# Revit family: Hager-GOLF-Flush_mounted-IP40-With_Cover-With_DIN-NoHosted-PT-pt
name_source: partatom
category: Electrical Equipment
units: mm (PartAtom-declared; Revit-internal decimal feet)

## family parameters
Always vertical = Yes
Cut with Voids When Loaded = No
Maintain Annotation Orientation = No
Panel Configuration = Two Columns, Circuits Across
Part Type = Panelboard
Room Calculation Point = No
Round Connector Dimension = Use Diameter
Shared = No
Work Plane-Based = Yes

## types (22) — shared parameters
Code hager = ADD-EC000214_EU
Default Elevation = 1200 mm
EF000003 - Mounting method = Flush-mounted
EF000007 - Colour = White
EF000024 - UV resistant = No
EF000049 - Depth = 97 mm  [stored 0.318241 ft]
EF000116 - RAL-number = 9010
EF000118 - With mounting plate = No
EF000218 - Built-in depth = 72 mm  [stored 0.23622 ft]
EF001062 - EMC-version = No
EF001088 - Extension possible = Yes
EF001134 - DIN-rail = Yes
EF004462 - Type of closure = Other
EF005474 - Degree of protection (IP) = IP40
EF006306 - With lock = No
EF009212 - Cover model = Closed
EF015776 - Earthing terminal block = Yes
EF015777 - Neutral terminal block = Yes
EF015941 - Signal passing door = Yes
ETIM class code = EC000214
ETIM class name = Small distribution board
HG000001-Number of columns = 1
HG000002-With door or cover = Yes
HG000003-Range = GOLF
HG000005-Thickness = 2 mm  [stored 0.00656168 ft]
HG000006-Flush mounted = Yes
HG000009-Double swing door = No
HG000010-Asymmetric doors = No
HG000011-Empty rows from bottom = No
HG000012-Door swing angle = 90.00°
HG000013-Door on the left = No
HG000014-Door on the right = Yes
HG000015-Clearance visibility = Yes
HG000016-Door 3D visibility = Yes
HG000017-Distance between poles = 18 mm  [stored 0.0590551 ft]
HG000060-RAL-number = 9010
HG000099-Onfly Template ID = 507532
Manufacturer = Hager
Name BIM&CO = Electricity
Name hager = ADD_Enclosures_EC000214
Reference = Template-Enclosure_EU-EC000214
Uniformat = Low Tension Service & Dist.
Uniformat code = D501001
zero-valued in all types: EF001131 - Inner depth, HG000007-Number of empty columns, HG000008-Number of empty rows

## per-type parameters (varying)
| type | BC_METADATA | EF000008 - Width | EF000040 - Height | EF000266 - Number of rows | EF000332 - Built-in height | EF000846 - Built-in width | EF002950 - Width in number of modular spacings | EF006244 - Transparent cover/door | HG000004-Manufacturer reference | HGEF000266-Number of rows | HGEF002950-Width in number of modular spacings |
| GOLF-Flush_mounted_W204_H225_D97_4_Modular_Spacing-VF104PP | {"ObjectGuid":"27fba677-e14b-473f-ab1f-916606832566","ModelGuid":"6b0a5d78-5159-40f6-8a03-57b23a842eb9","VariantGuid":"864c97b1-3ffa-4ff5-a66a-c80eaf7a0775","Revision":"#3","VariantName":"GOLF-Flush_mounted_W204_H225_D97_4_Modular_Spacing-VF104PP"} | 204 mm | 225 mm  [stored 0.738189 ft] | 1 | 189 mm  [stored 0.620079 ft] | 170 mm  [stored 0.557743 ft] | 4 | No | VF104PP | 1 | 4 |
| GOLF-Flush_mounted_W204_H225_D97_4_Modular_Spacing-VF104TP | {"ObjectGuid":"27fba677-e14b-473f-ab1f-916606832566","ModelGuid":"6b0a5d78-5159-40f6-8a03-57b23a842eb9","VariantGuid":"9f43bfa9-54e1-405c-b379-891d8edcb505","Revision":"#3","VariantName":"GOLF-Flush_mounted_W204_H225_D97_4_Modular_Spacing-VF104TP"} | 204 mm | 225 mm  [stored 0.738189 ft] | 1 | 189 mm  [stored 0.620079 ft] | 170 mm  [stored 0.557743 ft] | 4 | Yes | VF104TP | 1 | 4 |
| GOLF-Flush_mounted_W275_H225_D97_8_Modular_Spacing-VF108PP | {"ObjectGuid":"27fba677-e14b-473f-ab1f-916606832566","ModelGuid":"6b0a5d78-5159-40f6-8a03-57b23a842eb9","VariantGuid":"e941d9c0-3f43-46ef-aebe-78f6bd05ca91","Revision":"#3","VariantName":"GOLF-Flush_mounted_W275_H225_D97_8_Modular_Spacing-VF108PP"} | 275 mm | 225 mm  [stored 0.738189 ft] | 1 | 189 mm  [stored 0.620079 ft] | 242 mm | 8 | No | VF108PP | 1 | 8 |
| GOLF-Flush_mounted_W275_H225_D97_8_Modular_Spacing-VF108TP | {"ObjectGuid":"27fba677-e14b-473f-ab1f-916606832566","ModelGuid":"6b0a5d78-5159-40f6-8a03-57b23a842eb9","VariantGuid":"92c577ba-eb81-4f87-a642-f8e72ad0e866","Revision":"#3","VariantName":"GOLF-Flush_mounted_W275_H225_D97_8_Modular_Spacing-VF108TP"} | 275 mm | 225 mm  [stored 0.738189 ft] | 1 | 189 mm  [stored 0.620079 ft] | 242 mm | 8 | Yes | VF108TP | 1 | 8 |
| GOLF-Flush_mounted_W352_H293_D97_12_Modular_Spacing-VF112PP | {"ObjectGuid":"27fba677-e14b-473f-ab1f-916606832566","ModelGuid":"6b0a5d78-5159-40f6-8a03-57b23a842eb9","VariantGuid":"548664ed-063f-4b2a-900d-3e4a0788754e","Revision":"#3","VariantName":"GOLF-Flush_mounted_W352_H293_D97_12_Modular_Spacing-VF112PP"} | 352 mm | 293 mm | 1 | 257 mm | 318 mm | 12 | No | VF112PP | 1 | 12 |
| GOLF-Flush_mounted_W352_H293_D97_12_Modular_Spacing-VF112TP | {"ObjectGuid":"27fba677-e14b-473f-ab1f-916606832566","ModelGuid":"6b0a5d78-5159-40f6-8a03-57b23a842eb9","VariantGuid":"d2e3e115-dd0c-45f7-9bd5-f052c32fbd83","Revision":"#3","VariantName":"GOLF-Flush_mounted_W352_H293_D97_12_Modular_Spacing-VF112TP"} | 352 mm | 293 mm | 1 | 257 mm | 318 mm | 12 | Yes | VF112TP | 1 | 12 |
| GOLF-Flush_mounted_W460_H293_D97_18_Modular_Spacing-VF118PP | {"ObjectGuid":"27fba677-e14b-473f-ab1f-916606832566","ModelGuid":"6b0a5d78-5159-40f6-8a03-57b23a842eb9","VariantGuid":"3a656f87-a8f6-449d-a9c9-48a3a64e8f4a","Revision":"#3","VariantName":"GOLF-Flush_mounted_W460_H293_D97_18_Modular_Spacing-VF118PP"} | 460 mm | 293 mm | 1 | 257 mm | 426 mm | 18 | No | VF118PP | 1 | 18 |
| GOLF-Flush_mounted_W460_H293_D97_18_Modular_Spacing-VF118TP | {"ObjectGuid":"27fba677-e14b-473f-ab1f-916606832566","ModelGuid":"6b0a5d78-5159-40f6-8a03-57b23a842eb9","VariantGuid":"820288c5-0764-4536-8d23-105e28a68f0c","Revision":"#3","VariantName":"GOLF-Flush_mounted_W460_H293_D97_18_Modular_Spacing-VF118TP"} | 460 mm | 293 mm | 1 | 257 mm | 426 mm | 18 | Yes | VF118TP | 1 | 18 |
| GOLF-Flush_mounted_W532_H293_D97_22_Modular_Spacing-VF122PP | {"ObjectGuid":"27fba677-e14b-473f-ab1f-916606832566","ModelGuid":"6b0a5d78-5159-40f6-8a03-57b23a842eb9","VariantGuid":"9da77889-4c9e-4d81-bd8e-8231a7450184","Revision":"#3","VariantName":"GOLF-Flush_mounted_W532_H293_D97_22_Modular_Spacing-VF122PP"} | 532 mm | 293 mm | 1 | 257 mm | 498 mm  [stored 1.63386 ft] | 22 | No | VF122PP | 1 | 22 |
| GOLF-Flush_mounted_W532_H293_D97_22_Modular_Spacing-VF122TP | {"ObjectGuid":"27fba677-e14b-473f-ab1f-916606832566","ModelGuid":"6b0a5d78-5159-40f6-8a03-57b23a842eb9","VariantGuid":"ad5d6844-5be0-454a-a1fd-9d6e2aeff522","Revision":"#3","VariantName":"GOLF-Flush_mounted_W532_H293_D97_22_Modular_Spacing-VF122TP"} | 532 mm | 293 mm | 1 | 257 mm | 498 mm  [stored 1.63386 ft] | 22 | Yes | VF122TP | 1 | 22 |
| GOLF-Flush_mounted_W382_H418_D97_12_Modular_Spacing-VF212PP | {"ObjectGuid":"27fba677-e14b-473f-ab1f-916606832566","ModelGuid":"6b0a5d78-5159-40f6-8a03-57b23a842eb9","VariantGuid":"ab34e016-0eca-42d0-9cdb-4e88c6c8c064","Revision":"#3","VariantName":"GOLF-Flush_mounted_W382_H418_D97_12_Modular_Spacing-VF212PP"} | 382 mm | 418 mm | 2 | 382 mm | 318 mm | 12 | No | VF212PP | 2 | 12 |
| GOLF-Flush_mounted_W382_H418_D97_12_Modular_Spacing-VF212TP | {"ObjectGuid":"27fba677-e14b-473f-ab1f-916606832566","ModelGuid":"6b0a5d78-5159-40f6-8a03-57b23a842eb9","VariantGuid":"48db7ade-bad1-44e5-871f-5ca467f00f72","Revision":"#3","VariantName":"GOLF-Flush_mounted_W382_H418_D97_12_Modular_Spacing-VF212TP"} | 382 mm | 418 mm | 2 | 382 mm | 318 mm | 12 | Yes | VF212TP | 2 | 12 |
| GOLF-Flush_mounted_W460_H418_D97_18_Modular_Spacing-VF218PP | {"ObjectGuid":"27fba677-e14b-473f-ab1f-916606832566","ModelGuid":"6b0a5d78-5159-40f6-8a03-57b23a842eb9","VariantGuid":"6ce2cf06-d3ee-4dfe-a9e3-6ef3e52ed8d5","Revision":"#3","VariantName":"GOLF-Flush_mounted_W460_H418_D97_18_Modular_Spacing-VF218PP"} | 460 mm | 418 mm | 2 | 382 mm | 426 mm | 18 | No | VF218PP | 2 | 18 |
| GOLF-Flush_mounted_W460_H418_D97_18_Modular_Spacing-VF218TP | {"ObjectGuid":"27fba677-e14b-473f-ab1f-916606832566","ModelGuid":"6b0a5d78-5159-40f6-8a03-57b23a842eb9","VariantGuid":"48ca1aa4-2058-40bc-b18b-eb7a4535e2bc","Revision":"#3","VariantName":"GOLF-Flush_mounted_W460_H418_D97_18_Modular_Spacing-VF218TP"} | 460 mm | 418 mm | 2 | 382 mm | 426 mm | 18 | Yes | VF218TP | 2 | 18 |
| GOLF-Flush_mounted_W352_H543_D97_12_Modular_Spacing-VF312PP | {"ObjectGuid":"27fba677-e14b-473f-ab1f-916606832566","ModelGuid":"6b0a5d78-5159-40f6-8a03-57b23a842eb9","VariantGuid":"925867c6-1a86-4d49-a1d9-762615fed786","Revision":"#3","VariantName":"GOLF-Flush_mounted_W352_H543_D97_12_Modular_Spacing-VF312PP"} | 352 mm | 543 mm | 3 | 507 mm | 318 mm | 12 | No | VF312PP | 3 | 12 |
| GOLF-Flush_mounted_W352_H543_D97_12_Modular_Spacing-VF312TP | {"ObjectGuid":"27fba677-e14b-473f-ab1f-916606832566","ModelGuid":"6b0a5d78-5159-40f6-8a03-57b23a842eb9","VariantGuid":"7c8e6c8f-6477-4924-a157-5d5dcb0d6904","Revision":"#3","VariantName":"GOLF-Flush_mounted_W352_H543_D97_12_Modular_Spacing-VF312TP"} | 352 mm | 543 mm | 3 | 507 mm | 318 mm | 12 | Yes | VF312TP | 3 | 12 |
| GOLF-Flush_mounted_W460_H543_D97_18_Modular_Spacing-VF318PP | {"ObjectGuid":"27fba677-e14b-473f-ab1f-916606832566","ModelGuid":"6b0a5d78-5159-40f6-8a03-57b23a842eb9","VariantGuid":"6d162c79-f22d-4964-bfb8-bc0482c38eae","Revision":"#3","VariantName":"GOLF-Flush_mounted_W460_H543_D97_18_Modular_Spacing-VF318PP"} | 460 mm | 543 mm | 3 | 507 mm | 426 mm | 18 | No | VF318PP | 3 | 18 |
| GOLF-Flush_mounted_W460_H543_D97_18_Modular_Spacing-VF318TP | {"ObjectGuid":"27fba677-e14b-473f-ab1f-916606832566","ModelGuid":"6b0a5d78-5159-40f6-8a03-57b23a842eb9","VariantGuid":"6315e013-c1b3-45bf-8402-298b3d009cee","Revision":"#3","VariantName":"GOLF-Flush_mounted_W460_H543_D97_18_Modular_Spacing-VF318TP"} | 460 mm | 543 mm | 3 | 507 mm | 426 mm | 18 | Yes | VF318TP | 3 | 18 |
| GOLF-Flush_mounted_W352_H688_D97_12_Modular_Spacing-VF412PP | {"ObjectGuid":"27fba677-e14b-473f-ab1f-916606832566","ModelGuid":"6b0a5d78-5159-40f6-8a03-57b23a842eb9","VariantGuid":"58a577c8-08cd-4d8b-b5d5-deb31c42239b","Revision":"#3","VariantName":"GOLF-Flush_mounted_W352_H688_D97_12_Modular_Spacing-VF412PP"} | 352 mm | 688 mm | 4 | 652 mm | 318 mm | 12 | No | VF412PP | 4 | 12 |
| GOLF-Flush_mounted_W352_H688_D97_12_Modular_Spacing-VF412TP | {"ObjectGuid":"27fba677-e14b-473f-ab1f-916606832566","ModelGuid":"6b0a5d78-5159-40f6-8a03-57b23a842eb9","VariantGuid":"09560e6e-e228-402b-ae40-5888ca363ade","Revision":"#3","VariantName":"GOLF-Flush_mounted_W352_H688_D97_12_Modular_Spacing-VF412TP"} | 352 mm | 688 mm | 4 | 652 mm | 318 mm | 12 | Yes | VF412TP | 4 | 12 |
| GOLF-Flush_mounted_W460_H688_D97_18_Modular_Spacing-VF418PP | {"ObjectGuid":"27fba677-e14b-473f-ab1f-916606832566","ModelGuid":"6b0a5d78-5159-40f6-8a03-57b23a842eb9","VariantGuid":"fd781d83-8f81-42a6-9d59-9680d7bbcf99","Revision":"#3","VariantName":"GOLF-Flush_mounted_W460_H688_D97_18_Modular_Spacing-VF418PP"} | 460 mm | 688 mm | 4 | 652 mm | 426 mm | 18 | No | VF418PP | 4 | 18 |
| GOLF-Flush_mounted_W460_H688_D97_18_Modular_Spacing-VF418TP | {"ObjectGuid":"27fba677-e14b-473f-ab1f-916606832566","ModelGuid":"6b0a5d78-5159-40f6-8a03-57b23a842eb9","VariantGuid":"d05077de-2b96-4b83-a337-c94d77ba0f49","Revision":"#3","VariantName":"GOLF-Flush_mounted_W460_H688_D97_18_Modular_Spacing-VF418TP"} | 460 mm | 688 mm | 4 | 652 mm | 426 mm | 18 | Yes | VF418TP | 4 | 18 |

note: [stored X ft] marks values corroborated as IEEE doubles in the binary element streams (Revit-internal decimal feet)

## geometry (parser evidence)
native form markers: Sweep x12
no freeform markers — native parametric forms only
